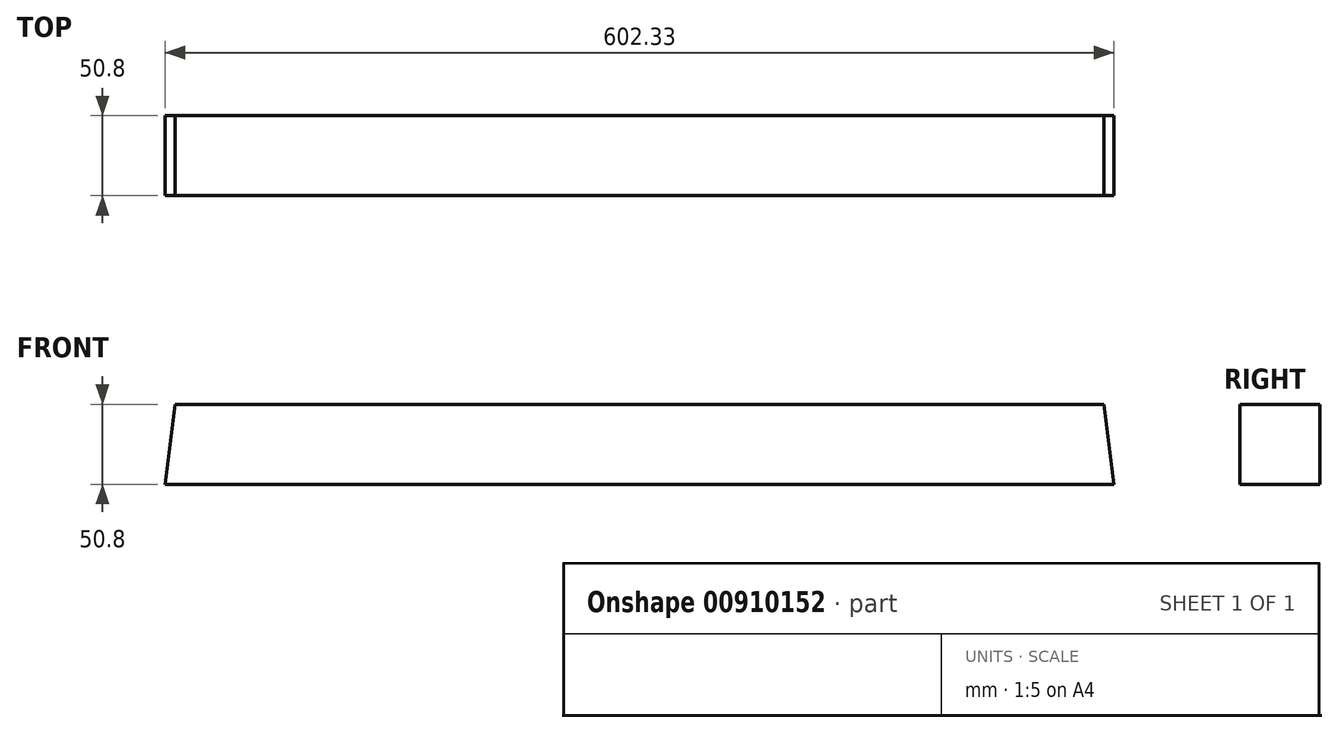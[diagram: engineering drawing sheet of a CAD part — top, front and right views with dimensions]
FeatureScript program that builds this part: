
annotation { "Feature Type Name" : "Feature", "Feature Type Description" : "" }
export const myFeature = defineFeature(function(context is Context, id is Id, definition is map)
    precondition{}
    {
        {
            var Q0;
            Q0=qCreatedBy(makeId("Front.planeOp"),FACE);
            var sketch = newSketch(context, id + "F0", { "sketchPlane" : qUnion([Q0])});
            skLineSegment(sketch, "E0.bottom", {"start": v(0, 0) * mm, "end": v(589.79, 0) * mm});
            skLineSegment(sketch, "E0.top", {"start": v(0, 50.8) * mm, "end": v(589.79, 50.8) * mm});
            skLineSegment(sketch, "E0.left", {"start": v(0, 0) * mm, "end": v(0, 50.8) * mm});
            skLineSegment(sketch, "E0.right", {"start": v(589.79, 0) * mm, "end": v(589.79, 50.8) * mm});
            skLineSegment(sketch, "E1", {"start": v(0, 50.8) * mm, "end": v(-6.27, 0) * mm});
            skLineSegment(sketch, "E2", {"start": v(-6.27, 0) * mm, "end": v(0, 0) * mm});
            skLineSegment(sketch, "E3", {"start": v(589.79, 0) * mm, "end": v(596.06, 0) * mm});
            skLineSegment(sketch, "E4", {"start": v(596.06, 0) * mm, "end": v(589.79, 50.8) * mm});
            skSolve(sketch);
        }
        {
            var Q0;
            Q0=makeQuery(id+"F0.imprint","IMPRINT",FACE,{"disambiguationData":[TD([[makeQuery(id+"F0.imprint","IMPRINT",EDGE,{"derivedFrom":sQuery(id+"F0.wireOp",EDGE,"E0.bottom")}),1.0]])]});
            extrude(context, id + "F1", {"entities" : qUnion([Q0]), "depth" : 50.8 * mm, "offsetDistance" : 25.4 * mm});
        }
        {
            var Q0;
            Q0=makeQuery(id+"F0.imprint","IMPRINT",FACE,{"disambiguationData":[TD([[makeQuery(id+"F0.imprint","IMPRINT",EDGE,{"derivedFrom":sQuery(id+"F0.wireOp",EDGE,"E0.right")}),-1.0]])]});
            extrude(context, id + "F2", {"entities" : qUnion([Q0]), "operationType" : NewBodyOperationType.ADD, "depth" : 50.8 * mm, "offsetDistance" : 25.4 * mm});
        }
        {
            var Q0;
            Q0=makeQuery(id+"F0.imprint","IMPRINT",FACE,{"disambiguationData":[TD([[makeQuery(id+"F0.imprint","IMPRINT",EDGE,{"derivedFrom":sQuery(id+"F0.wireOp",EDGE,"E0.left")}),1.0]])]});
            extrude(context, id + "F3", {"entities" : qUnion([Q0]), "operationType" : NewBodyOperationType.ADD, "depth" : 50.8 * mm, "offsetDistance" : 25.4 * mm});
        }
    });
